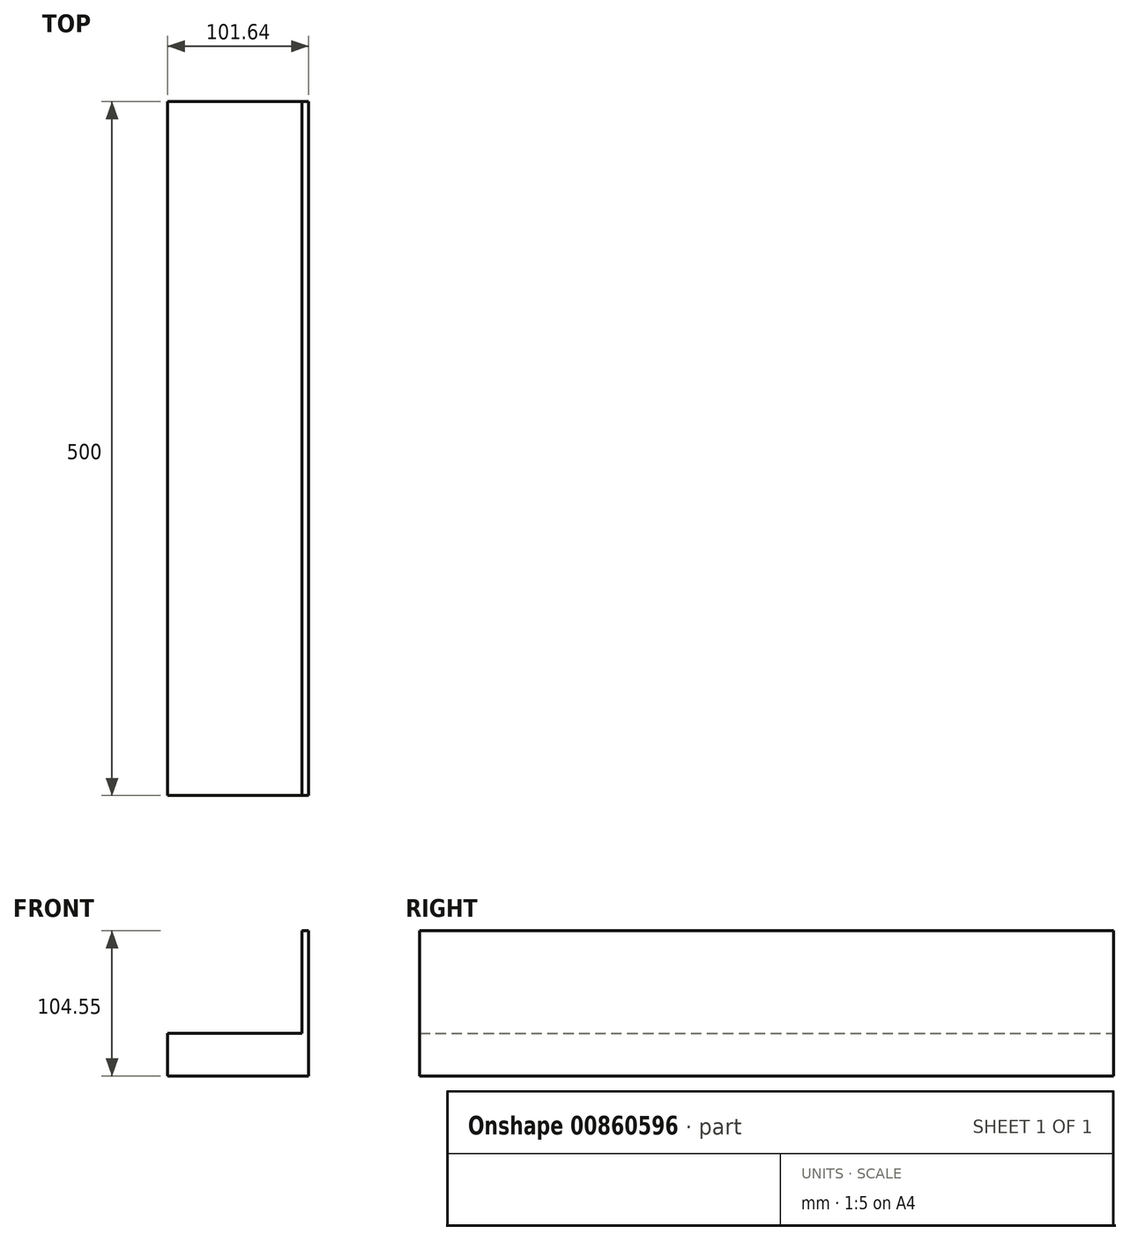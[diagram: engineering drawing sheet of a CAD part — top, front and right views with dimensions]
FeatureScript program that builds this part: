
annotation { "Feature Type Name" : "Feature", "Feature Type Description" : "" }
export const myFeature = defineFeature(function(context is Context, id is Id, definition is map)
    precondition{}
    {
        {
            var Q0;
            Q0=qCreatedBy(makeId("Front.planeOp"),FACE);
            var sketch = newSketch(context, id + "F0", { "sketchPlane" : qUnion([Q0])});
            skLineSegment(sketch, "E0.bottom", {"start": v(0, 0) * mm, "end": v(101.64, 0) * mm});
            skLineSegment(sketch, "E0.top", {"start": v(0, 30.82) * mm, "end": v(101.64, 30.82) * mm});
            skLineSegment(sketch, "E0.left", {"start": v(0, 0) * mm, "end": v(0, 30.82) * mm});
            skLineSegment(sketch, "E0.right", {"start": v(101.64, 0) * mm, "end": v(101.64, 30.82) * mm});
            skLineSegment(sketch, "E1.bottom", {"start": v(101.64, 30.82) * mm, "end": v(97, 30.82) * mm});
            skLineSegment(sketch, "E1.top", {"start": v(101.64, 104.55) * mm, "end": v(97, 104.55) * mm});
            skLineSegment(sketch, "E1.left", {"start": v(101.64, 30.82) * mm, "end": v(101.64, 104.55) * mm});
            skLineSegment(sketch, "E1.right", {"start": v(97, 30.82) * mm, "end": v(97, 104.55) * mm});
            skSolve(sketch);
        }
        {
            var Q0;
            Q0 = qSketchRegion(id + "F0", true);
            extrude(context, id + "F1", {"entities" : qUnion([Q0]), "depth" : 500 * mm, "offsetDistance" : 25 * mm});
        }
    });
